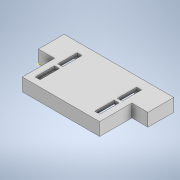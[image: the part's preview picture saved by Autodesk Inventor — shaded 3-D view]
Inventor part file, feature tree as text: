
AUTODESK INVENTOR PART (.ipt)
format: ipt  version: 2021 (Build 250183000, 183)  size: 166,400 bytes
history: native  units: in
note: dims shown in document units (in); Inventor stores cm internally (conversion verified against a paired STEP export)
features: sketch x4, extrude x3, projected_geometry x1
ambient origin geometry x8: Origin, YZ Plane, XZ Plane, XY Plane, X Axis, Y Axis, Z Axis, Center Point
bodies: Solid1 (feature_tree)
feature tree (8):
  extrude  "Extrusion1"  Depth=0.315in
  extrude  "Extrusion2"  Depth=0.2362in
  extrude  "Extrusion3"  Depth=0.3937in
  sketch  "Sketch4"  dims[d18=0.8661in d19=0.1181in d20=0.0in d21=0.0394in d22=0.0in d23=0.0394in d24=0.0394in d26=0.0591in d27=0.2362in d28=0.0394in d29=0.0591in d30=0.2362in d31=0.0394in d32=0.0394in d33=0.0591in d34=0.2362in d35=0.0394in d36=0.0394in d37=0.0in]
  sketch  "Sketch1"  dims[d0=1.3386in d1=0.315in]
  sketch  "Sketch2"  dims[d4=1.2598in d5=0.2362in]
  sketch  "Sketch3"  dims[d9=0.9449in d17=0.3937in]
  projected_geometry  "Projected Loop1"
